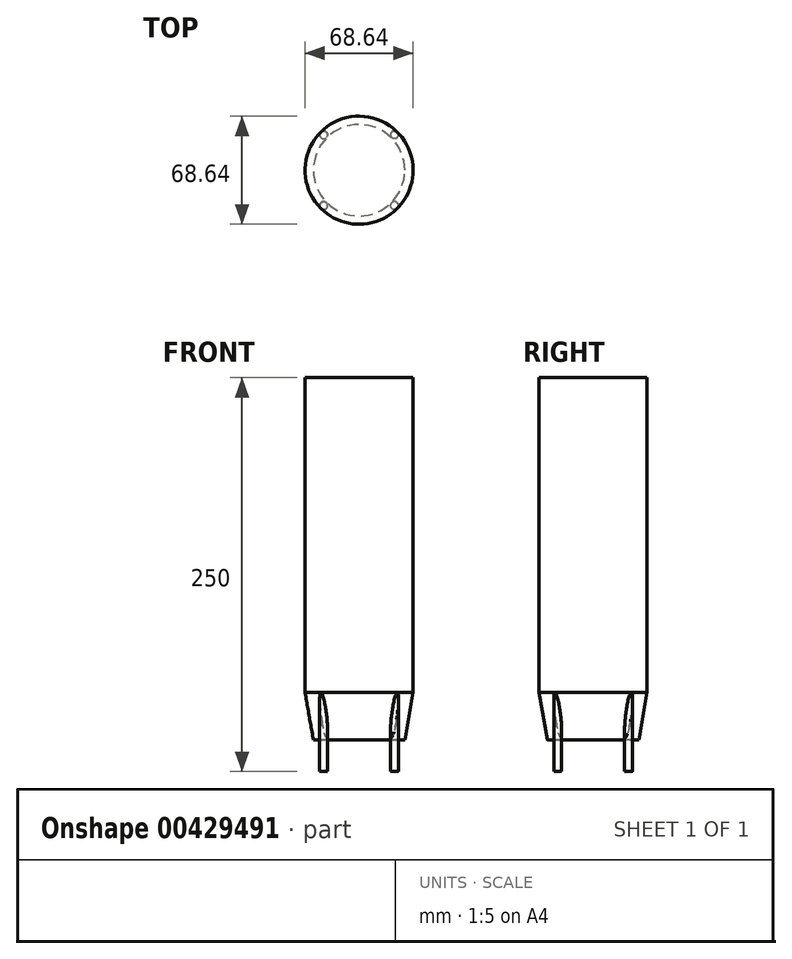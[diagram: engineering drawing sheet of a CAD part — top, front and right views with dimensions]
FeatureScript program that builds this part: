
annotation { "Feature Type Name" : "Feature", "Feature Type Description" : "" }
export const myFeature = defineFeature(function(context is Context, id is Id, definition is map)
    precondition{}
    {
        {
            var Q0;
            Q0=qCreatedBy(makeId("Top.planeOp"),FACE);
            var sketch = newSketch(context, id + "F0", { "sketchPlane" : qUnion([Q0])});
            skLineSegment(sketch, "E0.bottom", {"start": v(0, 0) * mm, "end": v(45, 0) * mm, "construction": true});
            skLineSegment(sketch, "E0.top", {"start": v(0, 45) * mm, "end": v(45, 45) * mm, "construction": true});
            skLineSegment(sketch, "E0.left", {"start": v(0, 0) * mm, "end": v(0, 45) * mm, "construction": true});
            skLineSegment(sketch, "E0.right", {"start": v(45, 0) * mm, "end": v(45, 45) * mm, "construction": true});
            skCircle(sketch, "E1", {"center": v(0, 45) * mm, "radius": 2.5 * mm});
            skCircle(sketch, "E2", {"center": v(45, 45) * mm, "radius": 2.5 * mm});
            skCircle(sketch, "E3", {"center": v(0, 0) * mm, "radius": 2.5 * mm});
            skCircle(sketch, "E4", {"center": v(45, 0) * mm, "radius": 2.5 * mm});
            skSolve(sketch);
        }
        {
            var Q0;
            Q0 = qSketchRegion(id + "F0", true);
            extrude(context, id + "F1", {"entities" : qUnion([Q0]), "depth" : 50 * mm});
        }
        {
            var Q0;
            Q0=makeQuery(id+"F1.opExtrude","CAP_FACE",FACE,{"disambiguationData":[OSD([sQuery(id+"F0.wireOp",EDGE,"E2")])],"isStart":false});
            var sketch = newSketch(context, id + "F2", { "sketchPlane" : qUnion([Q0])});
            skLineSegment(sketch, "E5", {"start": v(0, 0) * mm, "end": v(22.5, 0) * mm, "construction": true});
            skLineSegment(sketch, "E6", {"start": v(22.5, 0) * mm, "end": v(22.5, 22.5) * mm, "construction": true});
            skCircle(sketch, "E7", {"center": v(22.5, 22.5) * mm, "radius": 34.32 * mm});
            skSolve(sketch);
        }
        {
            var Q0;
            Q0 = qSketchRegion(id + "F2", true);
            extrude(context, id + "F3", {"entities" : qUnion([Q0]), "operationType" : NewBodyOperationType.ADD, "depth" : 200 * mm});
        }
        {
            var Q0;
            Q0=makeQuery(id+"F3.opExtrude","CAP_FACE",FACE,{"disambiguationData":[OSD([sQuery(id+"F2.wireOp",EDGE,"E7")])],"isStart":true});
            var sketch = newSketch(context, id + "F4", { "sketchPlane" : qUnion([Q0])});
            skCircle(sketch, "E8", {"center": v(22.5, -22.5) * mm, "radius": 34.32 * mm});
            skSolve(sketch);
        }
        {
            var Q0;
            Q0 = qSketchRegion(id + "F4", true);
            extrude(context, id + "F5", {"entities" : qUnion([Q0]), "operationType" : NewBodyOperationType.ADD, "depth" : 30 * mm, "hasDraft" : true, "draftAngle" : 10 * degree, "draftPullDirection" : true});
        }
    });
